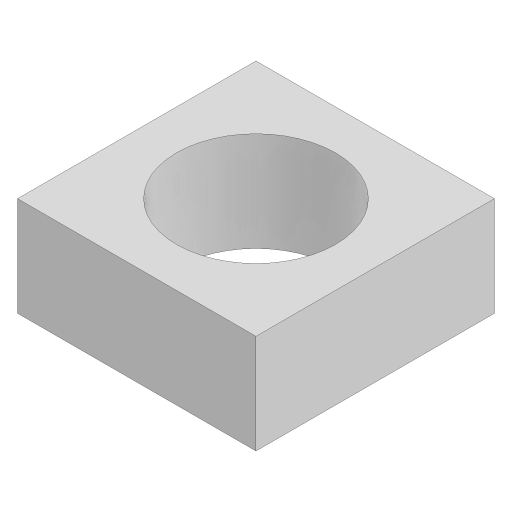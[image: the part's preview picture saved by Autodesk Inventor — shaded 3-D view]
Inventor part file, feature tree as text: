
AUTODESK INVENTOR PART (.ipt)
format: ipt  version: 2023 (Build 270158000, 158)  size: 190,464 bytes
history: native  units: mm
features: other x1, extrude x1, sketch x1
ambient origin geometry x8: Origin, YZ Plane, XZ Plane, XY Plane, X Axis, Y Axis, Z Axis, Center Point
bodies: Body1 (feature_tree)
feature tree (3):
  other  "솔리드1"
  extrude  "돌출1"  Depth=3.2mm
  sketch  "스케치1"
